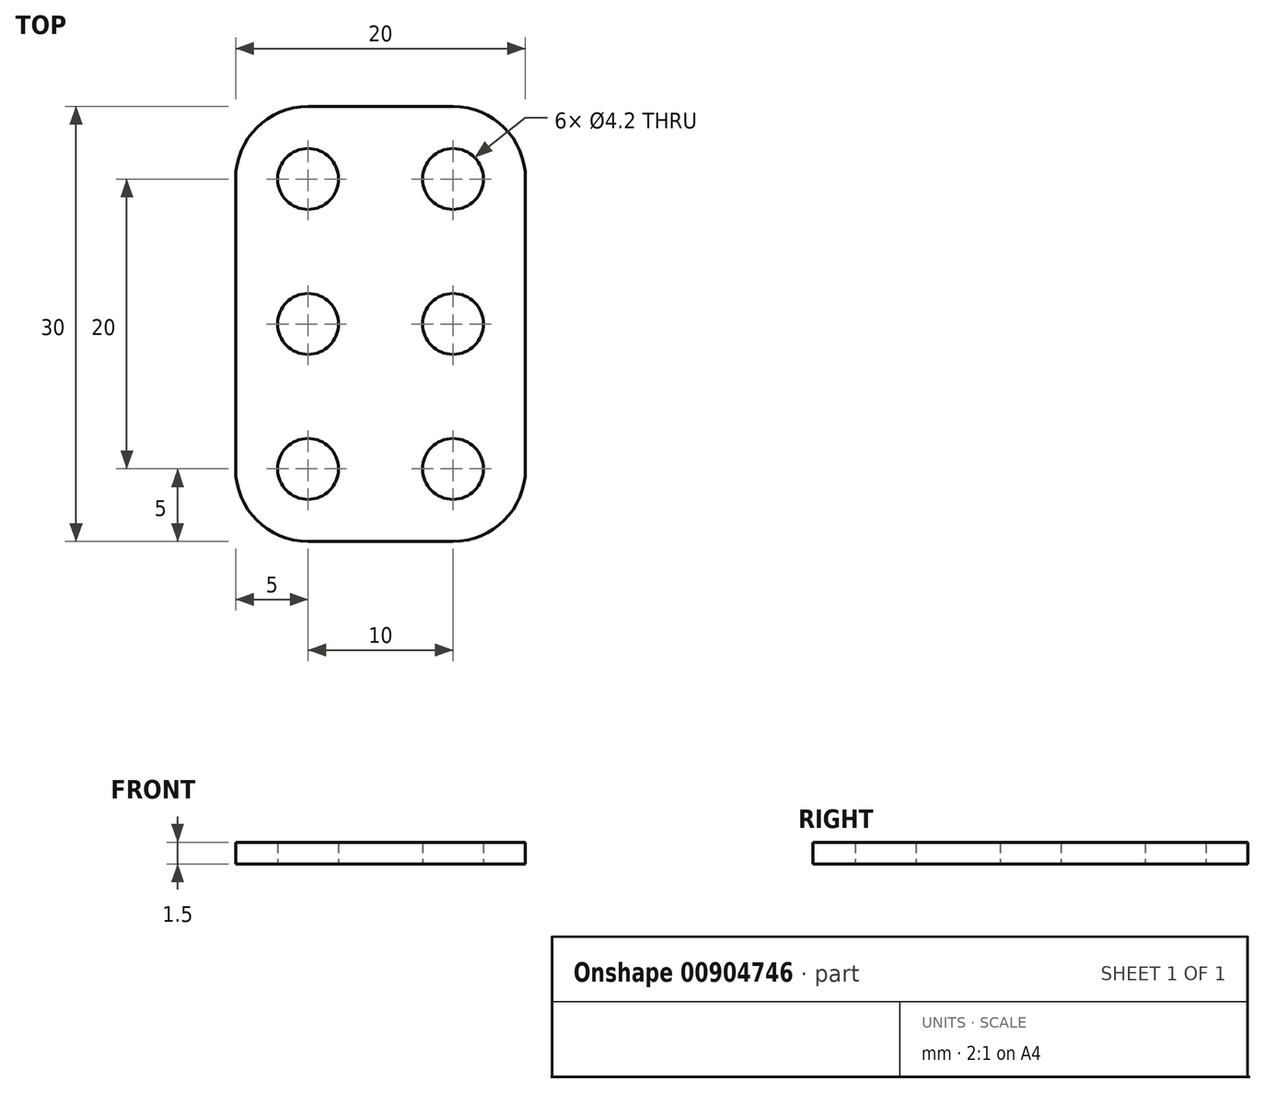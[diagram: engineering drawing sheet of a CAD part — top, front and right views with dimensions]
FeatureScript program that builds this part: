
annotation { "Feature Type Name" : "Feature", "Feature Type Description" : "" }
export const myFeature = defineFeature(function(context is Context, id is Id, definition is map)
    precondition{}
    {
        {
            var Q0;
            Q0=qCreatedBy(makeId("Top.planeOp"),FACE);
            var sketch = newSketch(context, id + "F0", { "sketchPlane" : qUnion([Q0])});
            skLineSegment(sketch, "E0.bottom", {"start": v(5, -15) * mm, "end": v(-5, -15) * mm});
            skLineSegment(sketch, "E0.top", {"start": v(5, 15) * mm, "end": v(-5, 15) * mm});
            skLineSegment(sketch, "E0.left", {"start": v(10, -10) * mm, "end": v(10, 10) * mm});
            skLineSegment(sketch, "E0.right", {"start": v(-10, -10) * mm, "end": v(-10, 10) * mm});
            skPoint(sketch, "E0.middle", {"position": v(0, 0) * mm});
            skPoint(sketch, "E1.visualSharp", {"position": v(-10, 15) * mm});
            skArc(sketch, "E1.filletArc", {"start": v(-5, 15) * mm, "mid": v(-8.54, 13.54) * mm, "end": v(-10, 10) * mm});
            skPoint(sketch, "E2.visualSharp", {"position": v(10, 15) * mm});
            skArc(sketch, "E2.filletArc", {"start": v(10, 10) * mm, "mid": v(8.54, 13.54) * mm, "end": v(5, 15) * mm});
            skPoint(sketch, "E3.visualSharp", {"position": v(10, -15) * mm});
            skArc(sketch, "E3.filletArc", {"start": v(5, -15) * mm, "mid": v(8.54, -13.54) * mm, "end": v(10, -10) * mm});
            skPoint(sketch, "E4.visualSharp", {"position": v(-10, -15) * mm});
            skArc(sketch, "E4.filletArc", {"start": v(-10, -10) * mm, "mid": v(-8.54, -13.54) * mm, "end": v(-5, -15) * mm});
            skCircle(sketch, "E5", {"center": v(-5, 10) * mm, "radius": 2.1 * mm});
            skCircle(sketch, "E6", {"center": v(5, 10) * mm, "radius": 2.1 * mm});
            skCircle(sketch, "E7", {"center": v(-5, -10) * mm, "radius": 2.1 * mm});
            skCircle(sketch, "E8", {"center": v(5, -10) * mm, "radius": 2.1 * mm});
            skLineSegment(sketch, "E9", {"start": v(5, 10) * mm, "end": v(5, -10) * mm, "construction": true});
            skLineSegment(sketch, "E10", {"start": v(-5, 10) * mm, "end": v(-5, -10) * mm, "construction": true});
            skCircle(sketch, "E11", {"center": v(-5, 0) * mm, "radius": 2.1 * mm});
            skCircle(sketch, "E12", {"center": v(5, 0) * mm, "radius": 2.1 * mm});
            skSolve(sketch);
        }
        {
            var Q0;
            Q0=makeQuery(id+"F0.imprint","IMPRINT",FACE,{"disambiguationData":[TD([[makeQuery(id+"F0.imprint","IMPRINT",EDGE,{"derivedFrom":sQuery(id+"F0.wireOp",EDGE,"E0.bottom")}),-1.0]])]});
            extrude(context, id + "F1", {"entities" : qUnion([Q0]), "depth" : 1.5 * mm, "offsetDistance" : 25 * mm});
        }
    });
